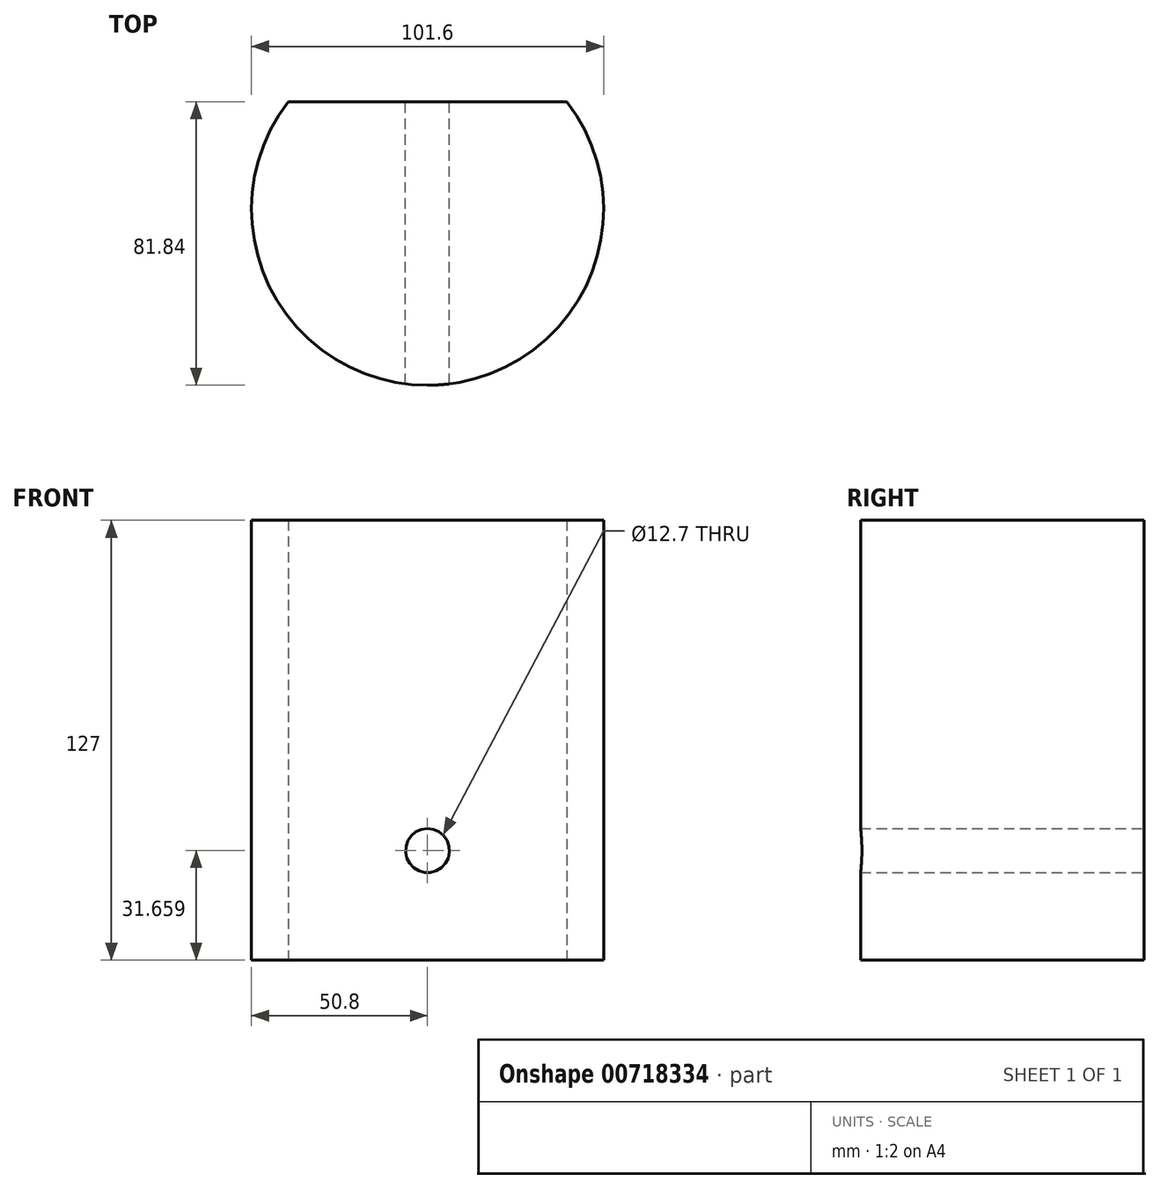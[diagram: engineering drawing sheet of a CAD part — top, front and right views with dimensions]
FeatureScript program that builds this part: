
annotation { "Feature Type Name" : "Feature", "Feature Type Description" : "" }
export const myFeature = defineFeature(function(context is Context, id is Id, definition is map)
    precondition{}
    {
        {
            var Q0;
            Q0=qCreatedBy(makeId("Top.planeOp"),FACE);
            var sketch = newSketch(context, id + "F0", { "sketchPlane" : qUnion([Q0])});
            skArc(sketch, "E0", {"start": v(-40.22, 31.04) * mm, "mid": v(0, -50.8) * mm, "end": v(40.22, 31.04) * mm});
            skLineSegment(sketch, "E1", {"start": v(-40.22, 31.04) * mm, "end": v(40.22, 31.04) * mm});
            skSolve(sketch);
        }
        {
            var Q0;
            Q0 = qSketchRegion(id + "F0", true);
            extrude(context, id + "F1", {"entities" : qUnion([Q0]), "depth" : 127 * mm, "offsetDistance" : 25.4 * mm});
        }
        {
            var Q0;
            Q0=makeQuery(id+"F1.opExtrude","SWEPT_FACE",FACE,{"disambiguationData":[OSD([sQuery(id+"F0.wireOp",EDGE,"E1")])]});
            var sketch = newSketch(context, id + "F2", { "sketchPlane" : qUnion([Q0])});
            skCircle(sketch, "E2", {"center": v(0, 31.66) * mm, "radius": 6.35 * mm});
            skSolve(sketch);
        }
        {
            var Q0;
            Q0 = qSketchRegion(id + "F2", true);
            extrude(context, id + "F3", {"entities" : qUnion([Q0]), "operationType" : NewBodyOperationType.REMOVE, "oppositeDirection" : true, "depth" : 127 * mm, "offsetDistance" : 25.4 * mm});
        }
    });
